# Revit family: Urinal_Washdown-Top_Spud-American_Standard-Washbrook-6590_Series
name_source: partatom
category: Plumbing Fixtures
revit_build: Autodesk Revit 2018 (Build: 20170223_1515(x64)
units: mm (PartAtom-declared; Revit-internal decimal feet)

## family parameters
Cut with Voids When Loaded = No
Host = Face
OmniClass Number = 23.45.05.21.11.21
OmniClass Title = Urinals
Part Type = Normal
Room Calculation Point = No
Round Connector Dimension = Use Radius
Shared = Yes

## types (2) — shared parameters
ADA Compliant = Yes
Assembly Code = D2010210
CW Connection = Yes
CWFU = 5
Cold Water Connection Diameter = 3/4"
Cold Water Connection Height = 11 1/2"
Cold Water Connection Radius = 3/8"
Cold Water Connection Width = 4 3/4"
Default Elevation = 17"
Finish = Vitreous China-American Standard-020-White
Flush Rate = 0.125-1.0gpf (0.5-3.8Lpf)
HW Connection = No
Height = 18"
IAPMO Compliance = ASME A112.19.2-2008/CSA B45.1-08 for Vitreous China Fixtures
Installation Type = Wall Mounted
Length = 14 1/8"
Manufacturer = American Standard
Material = Vitreous China-American Standard-020-White
Price = Prices may vary. Please consult Manufacturer Representative for most up-to-date price list.
Product Documentation Link = https://americanstandard.box.com
Product Page URL = https://www.americanstandard-us.com
Recommended Working Pressure = between 20 psi at valve when flushing and 80 psi static
Revised Date = 09/29/2021
Shipping Weight = 56lbs (25.3kg)
URL = http://www.americanstandard-us.com
Vent Connection = No
WFU = 5
Warranty Information = 1 Year Limited Warranty
Waste Connection = Yes
Waste Connection Diameter = 2"
Waste Connection Height = 20 1/2"
Waste Connection Radius = 1"
Width = 18 7/8"
zero-valued in all types: HWFU

## per-type parameters (varying)
| type | Description |
| 6590001.020 | Washbrook  FloWise Washout Top Spud Urinal. |
| 6590001EC.020 | Washbrook  FloWise Washout Top Spud Urinal Everclean. |

note: column(s) folded — value = type name in every type: Model

## geometry (parser evidence)
native form markers: Sweep x2
no freeform markers — native parametric forms only
